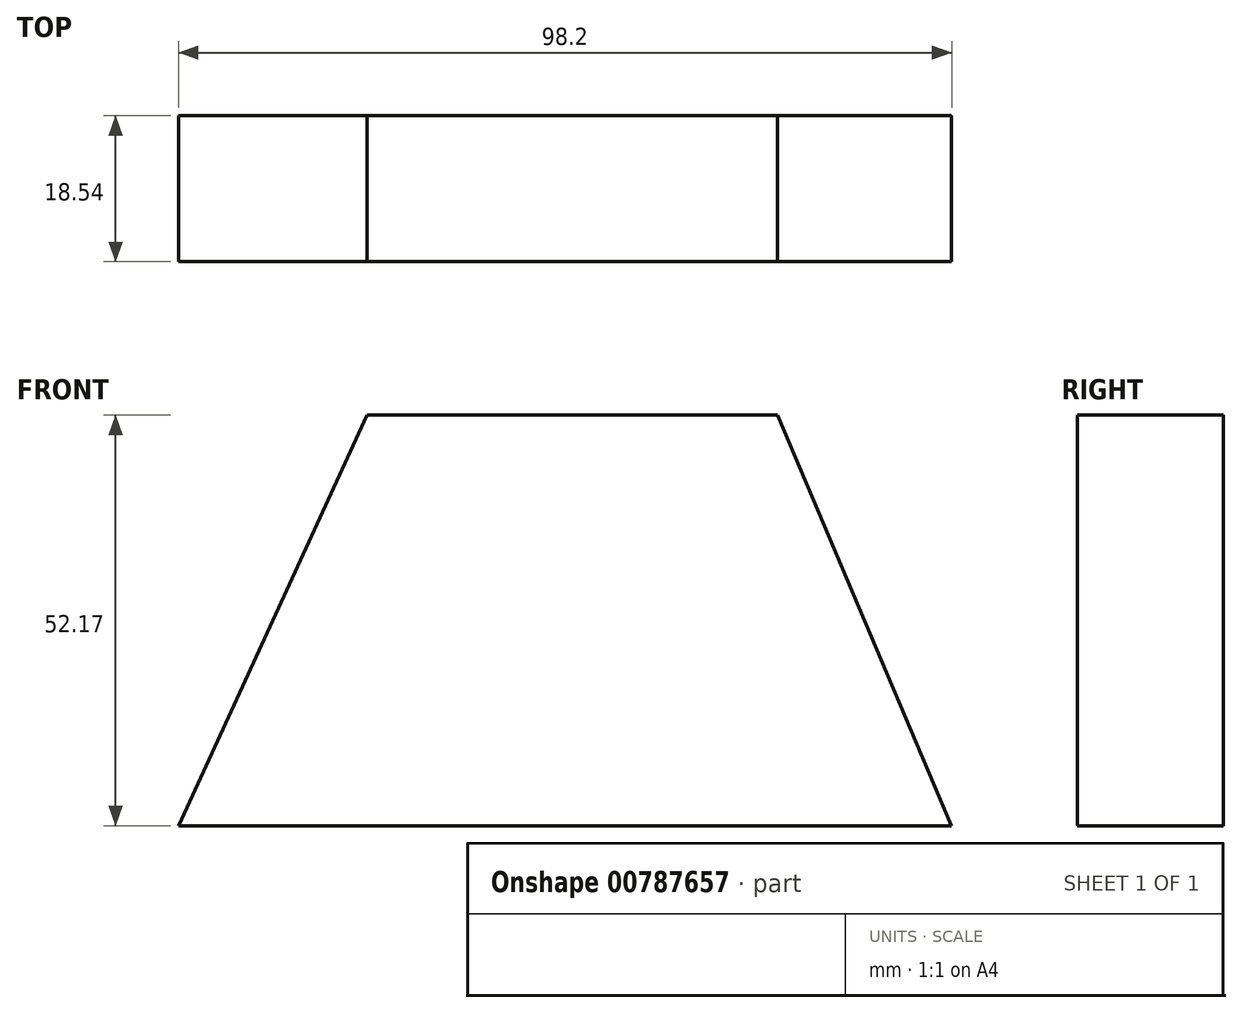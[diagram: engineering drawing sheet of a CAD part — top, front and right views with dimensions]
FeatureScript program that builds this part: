
annotation { "Feature Type Name" : "Feature", "Feature Type Description" : "" }
export const myFeature = defineFeature(function(context is Context, id is Id, definition is map)
    precondition{}
    {
        {
            var Q0;
            Q0=qCreatedBy(makeId("Front.planeOp"),FACE);
            var sketch = newSketch(context, id + "F0", { "sketchPlane" : qUnion([Q0])});
            skLineSegment(sketch, "E0", {"start": v(-49.38, 0) * mm, "end": v(48.82, 0) * mm});
            skLineSegment(sketch, "E1", {"start": v(48.82, 0) * mm, "end": v(26.72, 52.17) * mm});
            skLineSegment(sketch, "E2", {"start": v(26.72, 52.17) * mm, "end": v(-25.46, 52.17) * mm});
            skLineSegment(sketch, "E3", {"start": v(-25.46, 52.17) * mm, "end": v(-49.38, 0) * mm});
            skSolve(sketch);
        }
        {
            var Q0;
            Q0=makeQuery(id+"F0.imprint","IMPRINT",FACE,{"disambiguationData":[TD([[makeQuery(id+"F0.imprint","IMPRINT",EDGE,{"derivedFrom":sQuery(id+"F0.wireOp",EDGE,"E0")}),1.0]])]});
            extrude(context, id + "F1", {"entities" : qUnion([Q0]), "depth" : 18.54 * mm, "offsetDistance" : 25.4 * mm});
        }
    });
